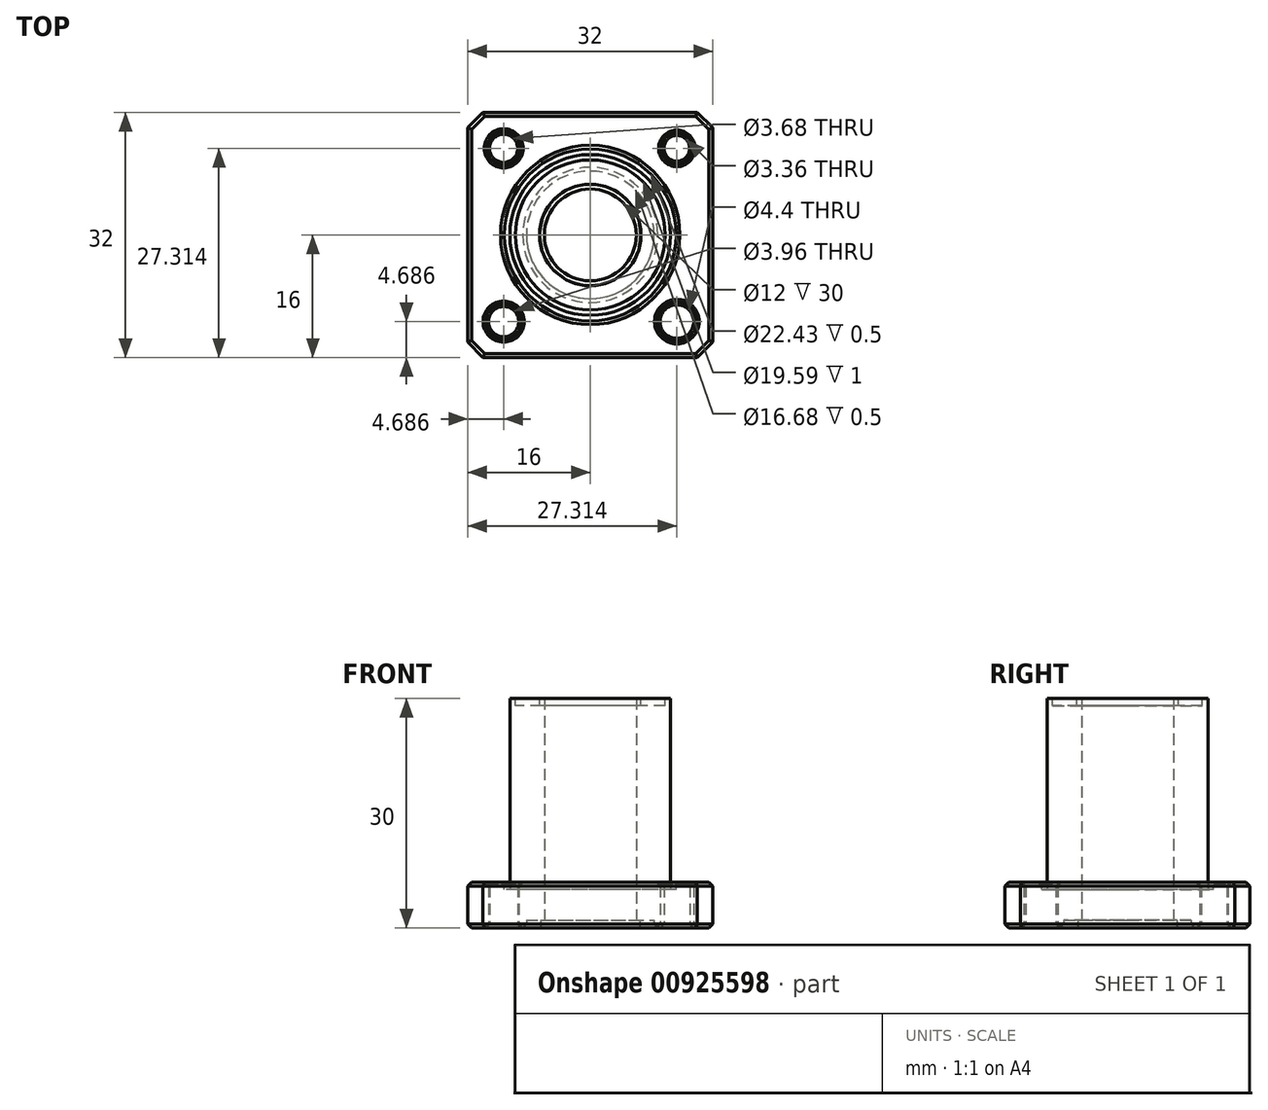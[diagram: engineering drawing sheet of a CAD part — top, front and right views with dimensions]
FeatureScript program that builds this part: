
annotation { "Feature Type Name" : "Feature", "Feature Type Description" : "" }
export const myFeature = defineFeature(function(context is Context, id is Id, definition is map)
    precondition{}
    {
        {
            var Q0;
            Q0=qCreatedBy(makeId("Top.planeOp"),FACE);
            var sketch = newSketch(context, id + "F0", { "sketchPlane" : qUnion([Q0])});
            skLineSegment(sketch, "E0.bottom", {"start": v(16, -16) * mm, "end": v(-16, -16) * mm});
            skLineSegment(sketch, "E0.top", {"start": v(16, 16) * mm, "end": v(-16, 16) * mm});
            skLineSegment(sketch, "E0.left", {"start": v(16, -16) * mm, "end": v(16, 16) * mm});
            skLineSegment(sketch, "E0.right", {"start": v(-16, -16) * mm, "end": v(-16, 16) * mm});
            skPoint(sketch, "E0.middle", {"position": v(0, 0) * mm});
            skCircle(sketch, "E1", {"center": v(0, 0) * mm, "radius": 16 * mm, "construction": true});
            skLineSegment(sketch, "E2", {"start": v(-16, 16) * mm, "end": v(16, -16) * mm, "construction": true});
            skLineSegment(sketch, "E3", {"start": v(16, 16) * mm, "end": v(-16, -16) * mm, "construction": true});
            skCircle(sketch, "E4", {"center": v(-11.31, 11.31) * mm, "radius": 1.84 * mm});
            skCircle(sketch, "E5", {"center": v(11.31, 11.31) * mm, "radius": 1.68 * mm});
            skCircle(sketch, "E6", {"center": v(11.31, -11.31) * mm, "radius": 2.2 * mm});
            skCircle(sketch, "E7", {"center": v(-11.31, -11.31) * mm, "radius": 1.98 * mm});
            skCircle(sketch, "E8", {"center": v(0, 0) * mm, "radius": 6 * mm});
            skSolve(sketch);
        }
        {
            var Q0;
            Q0=makeQuery(id+"F0.imprint","IMPRINT",FACE,{"disambiguationData":[TD([[makeQuery(id+"F0.imprint","IMPRINT",EDGE,{"derivedFrom":sQuery(id+"F0.wireOp",EDGE,"E0.bottom")}),-1.0]])]});
            extrude(context, id + "F1", {"entities" : qUnion([Q0]), "depth" : 6 * mm, "offsetDistance" : 25 * mm});
        }
        {
            var Q0;
            Q0=makeQuery(id+"F1.opExtrude","CAP_FACE",FACE,{"disambiguationData":[OSD([sQuery(id+"F0.wireOp",EDGE,"E0.bottom"),sQuery(id+"F0.wireOp",EDGE,"E0.top"),sQuery(id+"F0.wireOp",EDGE,"E0.left"),sQuery(id+"F0.wireOp",EDGE,"E0.right"),sQuery(id+"F0.wireOp",EDGE,"E4"),sQuery(id+"F0.wireOp",EDGE,"E5"),sQuery(id+"F0.wireOp",EDGE,"E6"),sQuery(id+"F0.wireOp",EDGE,"E7"),sQuery(id+"F0.wireOp",EDGE,"E8")])],"isStart":false});
            var sketch = newSketch(context, id + "F2", { "sketchPlane" : qUnion([Q0])});
            skCircle(sketch, "E9", {"center": v(0, 0) * mm, "radius": 10.5 * mm});
            skCircle(sketch, "E10.0", {"center": v(0, 0) * mm, "radius": 6 * mm});
            skSolve(sketch);
        }
        {
            var Q0;
            Q0 = qSketchRegion(id + "F2", true);
            extrude(context, id + "F3", {"entities" : qUnion([Q0]), "operationType" : NewBodyOperationType.ADD, "depth" : 24 * mm, "offsetDistance" : 25 * mm});
        }
        {
            var Q0;
            Q0=makeQuery(id+"F1.opExtrude","SWEPT_EDGE",EDGE,{"disambiguationData":[OSD([sQuery(id+"F0.wireOp",EDGE,"E0.bottom"),sQuery(id+"F0.wireOp",EDGE,"E0.right")])]});
            var Q1;
            Q1=makeQuery(id+"F1.opExtrude","SWEPT_EDGE",EDGE,{"disambiguationData":[OSD([sQuery(id+"F0.wireOp",EDGE,"E0.bottom"),sQuery(id+"F0.wireOp",EDGE,"E0.left")])]});
            var Q2;
            Q2=makeQuery(id+"F1.opExtrude","SWEPT_EDGE",EDGE,{"disambiguationData":[OSD([sQuery(id+"F0.wireOp",EDGE,"E0.top"),sQuery(id+"F0.wireOp",EDGE,"E0.right")])]});
            var Q3;
            Q3=makeQuery(id+"F1.opExtrude","SWEPT_EDGE",EDGE,{"disambiguationData":[OSD([sQuery(id+"F0.wireOp",EDGE,"E0.top"),sQuery(id+"F0.wireOp",EDGE,"E0.left")])]});
            chamfer(context, id + "F4", {"entities" : qUnion([Q0, Q1, Q2, Q3]), "width" : 2 * mm, "tangentPropagation" : true});
        }
        {
            var Q0;
            Q0=makeQuery(id+"F1.opExtrude","CAP_FACE",FACE,{"disambiguationData":[OSD([sQuery(id+"F0.wireOp",EDGE,"E0.bottom"),sQuery(id+"F0.wireOp",EDGE,"E0.top"),sQuery(id+"F0.wireOp",EDGE,"E0.left"),sQuery(id+"F0.wireOp",EDGE,"E0.right"),sQuery(id+"F0.wireOp",EDGE,"E4"),sQuery(id+"F0.wireOp",EDGE,"E5"),sQuery(id+"F0.wireOp",EDGE,"E6"),sQuery(id+"F0.wireOp",EDGE,"E7"),sQuery(id+"F0.wireOp",EDGE,"E8")])],"isStart":false});
            var sketch = newSketch(context, id + "F5", { "sketchPlane" : qUnion([Q0])});
            skCircle(sketch, "E11", {"center": v(0, 0) * mm, "radius": 11.21 * mm});
            skCircle(sketch, "E12.0", {"center": v(0, 0) * mm, "radius": 10.5 * mm});
            skSolve(sketch);
        }
        {
            var Q0;
            Q0 = qSketchRegion(id + "F5", true);
            extrude(context, id + "F6", {"entities" : qUnion([Q0]), "operationType" : NewBodyOperationType.REMOVE, "oppositeDirection" : true, "depth" : 1 * mm, "offsetDistance" : 25 * mm});
        }
        {
            var Q0;
            Q0=makeQuery(id+"F3.opExtrude","CAP_FACE",FACE,{"disambiguationData":[OSD([sQuery(id+"F2.wireOp",EDGE,"E9"),sQuery(id+"F2.wireOp",EDGE,"E10.0")])],"isStart":false});
            var sketch = newSketch(context, id + "F7", { "sketchPlane" : qUnion([Q0])});
            skCircle(sketch, "E13", {"center": v(0, 0) * mm, "radius": 6.63 * mm});
            skCircle(sketch, "E14", {"center": v(0, 0) * mm, "radius": 9.8 * mm});
            skSolve(sketch);
        }
        {
            var Q0;
            Q0 = qSketchRegion(id + "F7", true);
            extrude(context, id + "F8", {"entities" : qUnion([Q0]), "operationType" : NewBodyOperationType.REMOVE, "oppositeDirection" : true, "depth" : 1 * mm, "offsetDistance" : 25 * mm});
        }
        {
            var Q0;
            Q0=makeQuery(id+"F1.opExtrude","CAP_EDGE",EDGE,{"disambiguationData":[OSD([sQuery(id+"F0.wireOp",EDGE,"E7")])],"isStart":false});
            var Q1;
            Q1=makeQuery(id+"F1.opExtrude","CAP_EDGE",EDGE,{"disambiguationData":[OSD([sQuery(id+"F0.wireOp",EDGE,"E5")])],"isStart":false});
            var Q2;
            Q2=makeQuery(id+"F1.opExtrude","CAP_EDGE",EDGE,{"disambiguationData":[OSD([sQuery(id+"F0.wireOp",EDGE,"E6")])],"isStart":false});
            var Q3;
            Q3=makeQuery(id+"F1.opExtrude","CAP_EDGE",EDGE,{"disambiguationData":[OSD([sQuery(id+"F0.wireOp",EDGE,"E4")])],"isStart":false});
            chamfer(context, id + "F9", {"entities" : qUnion([Q0, Q1, Q2, Q3]), "width" : .5 * mm, "tangentPropagation" : true});
        }
        {
            var Q0;
            Q0=makeQuery(id+"F1.opExtrude","CAP_FACE",FACE,{"disambiguationData":[OSD([sQuery(id+"F0.wireOp",EDGE,"E0.bottom"),sQuery(id+"F0.wireOp",EDGE,"E0.top"),sQuery(id+"F0.wireOp",EDGE,"E0.left"),sQuery(id+"F0.wireOp",EDGE,"E0.right"),sQuery(id+"F0.wireOp",EDGE,"E4"),sQuery(id+"F0.wireOp",EDGE,"E5"),sQuery(id+"F0.wireOp",EDGE,"E6"),sQuery(id+"F0.wireOp",EDGE,"E7"),sQuery(id+"F0.wireOp",EDGE,"E8")])],"isStart":true});
            var sketch = newSketch(context, id + "F10", { "sketchPlane" : qUnion([Q0])});
            skCircle(sketch, "E15", {"center": v(0, 0) * mm, "radius": 6.48 * mm});
            skCircle(sketch, "E16", {"center": v(0, 0) * mm, "radius": 8.34 * mm});
            skSolve(sketch);
        }
        {
            var Q0;
            Q0 = qSketchRegion(id + "F10", true);
            extrude(context, id + "F11", {"entities" : qUnion([Q0]), "operationType" : NewBodyOperationType.REMOVE, "oppositeDirection" : true, "depth" : 1 * mm, "offsetDistance" : 25 * mm});
        }
        {
            var Q0;
            {var subQ0=sQuery(id+"F0.wireOp",EDGE,"E0.right");var subQ1=sQuery(id+"F0.wireOp",EDGE,"E0.bottom");var subQ2=sQuery(id+"F0.wireOp",EDGE,"E0.left");var subQ3=sQuery(id+"F0.wireOp",EDGE,"E7");var subQ4=sQuery(id+"F0.wireOp",EDGE,"E6");var subQ5=sQuery(id+"F0.wireOp",EDGE,"E5");var subQ6=sQuery(id+"F0.wireOp",EDGE,"E4");var subQ7=sQuery(id+"F0.wireOp",EDGE,"E0.top");Q0=makeQuery(id+"F11.boolean.opBoolean","SPLIT",FACE,{"disambiguationData":[TD([makeQuery(id+"F1.opExtrude","SWEPT_FACE",FACE,{"disambiguationData":[OSD([subQ1])]})])],"derivedFrom":makeQuery(id+"F1.opExtrude","CAP_FACE",FACE,{"disambiguationData":[OSD([subQ1,subQ7,subQ2,subQ0,subQ6,subQ5,subQ4,subQ3,sQuery(id+"F0.wireOp",EDGE,"E8")])],"isStart":true})});}
            var Q1;
            Q1=makeQuery(id+"F1.opExtrude","CAP_FACE",FACE,{"disambiguationData":[OSD([sQuery(id+"F0.wireOp",EDGE,"E0.bottom"),sQuery(id+"F0.wireOp",EDGE,"E0.top"),sQuery(id+"F0.wireOp",EDGE,"E0.left"),sQuery(id+"F0.wireOp",EDGE,"E0.right"),sQuery(id+"F0.wireOp",EDGE,"E4"),sQuery(id+"F0.wireOp",EDGE,"E5"),sQuery(id+"F0.wireOp",EDGE,"E6"),sQuery(id+"F0.wireOp",EDGE,"E7"),sQuery(id+"F0.wireOp",EDGE,"E8")])],"isStart":false});
            chamfer(context, id + "F12", {"entities" : qUnion([Q0, Q1]), "width" : .5 * mm, "tangentPropagation" : true});
        }
    });
